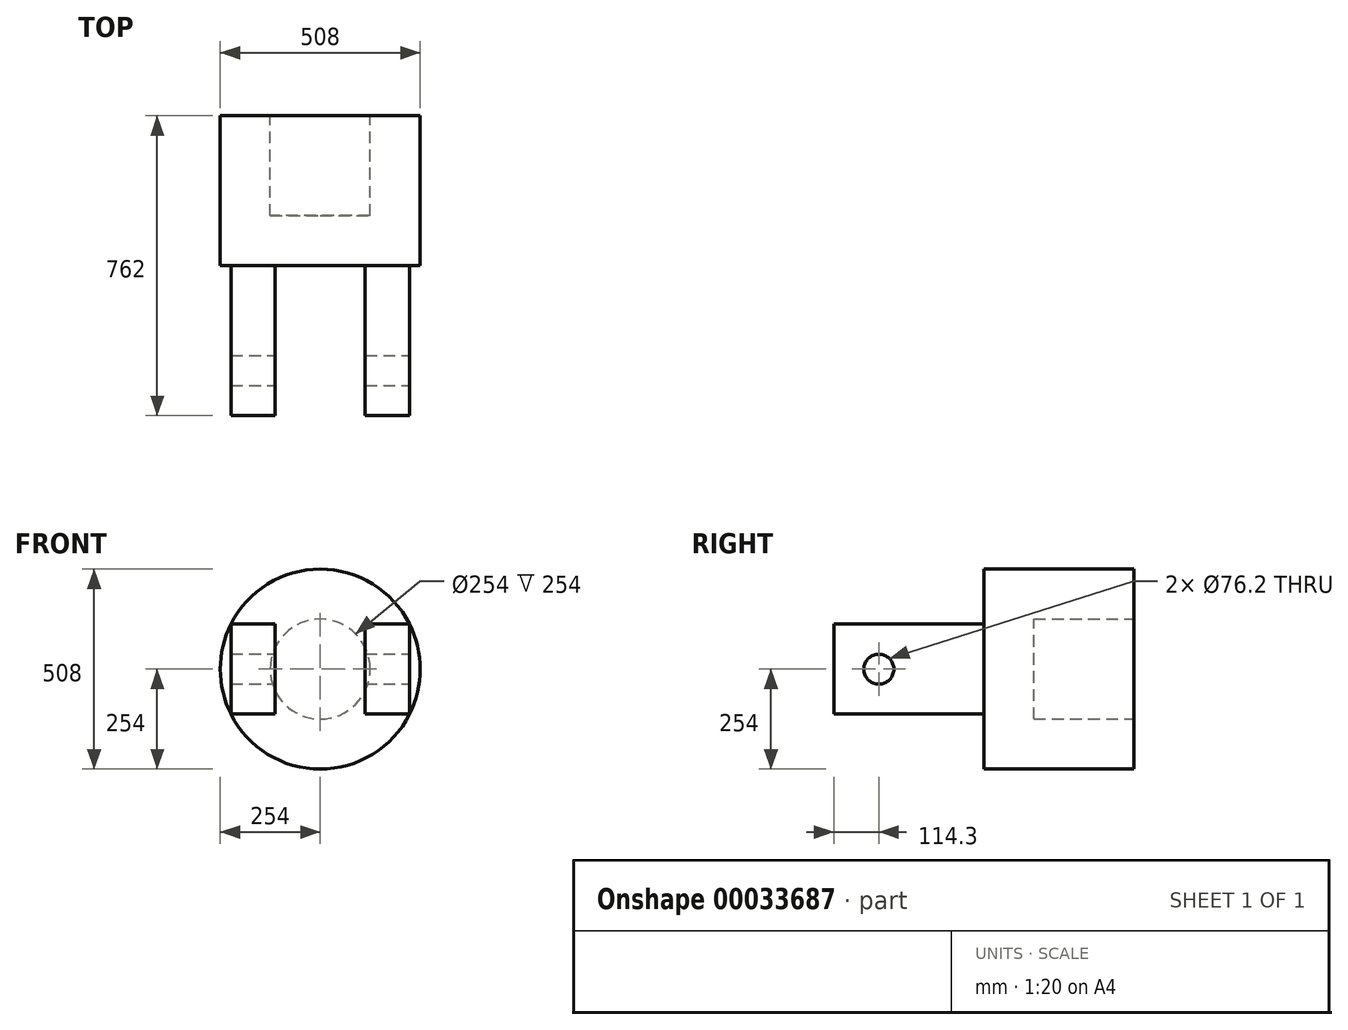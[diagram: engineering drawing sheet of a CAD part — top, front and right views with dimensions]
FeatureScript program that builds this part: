
annotation { "Feature Type Name" : "Feature", "Feature Type Description" : "" }
export const myFeature = defineFeature(function(context is Context, id is Id, definition is map)
    precondition{}
    {
        {
            var Q0;
            Q0=qCreatedBy(makeId("Front.planeOp"),FACE);
            var sketch = newSketch(context, id + "F0", { "sketchPlane" : qUnion([Q0])});
            skCircle(sketch, "E0", {"center": v(0, 0) * mm, "radius": 127 * mm});
            skCircle(sketch, "E1", {"center": v(0, 0) * mm, "radius": 254 * mm});
            skSolve(sketch);
        }
        {
            var Q0;
            Q0 = qSketchRegion(id + "F0", true);
            extrude(context, id + "F1", {"entities" : qUnion([Q0]), "depth" : 254 * mm});
        }
        {
            var Q0;
            Q0=makeQuery(id+"F1.opExtrude","CAP_FACE",FACE,{"disambiguationData":[OSD([sQuery(id+"F0.wireOp",EDGE,"E0"),sQuery(id+"F0.wireOp",EDGE,"E1")])],"isStart":false});
            var sketch = newSketch(context, id + "F2", { "sketchPlane" : qUnion([Q0])});
            skCircle(sketch, "E2", {"center": v(0, 0) * mm, "radius": 254 * mm});
            skSolve(sketch);
        }
        {
            var Q0;
            Q0 = qSketchRegion(id + "F2", true);
            extrude(context, id + "F3", {"entities" : qUnion([Q0]), "operationType" : NewBodyOperationType.ADD, "depth" : 127 * mm});
        }
        {
            var Q0;
            Q0=makeQuery(id+"F3.opExtrude","CAP_FACE",FACE,{"disambiguationData":[OSD([sQuery(id+"F2.wireOp",EDGE,"E2")])],"isStart":false});
            var sketch = newSketch(context, id + "F4", { "sketchPlane" : qUnion([Q0])});
            skLineSegment(sketch, "E3.bottom", {"start": v(-226.83, 114.3) * mm, "end": v(-114.3, 114.3) * mm});
            skLineSegment(sketch, "E3.top", {"start": v(-226.83, -114.3) * mm, "end": v(-114.3, -114.3) * mm});
            skLineSegment(sketch, "E3.left", {"start": v(-226.83, 114.3) * mm, "end": v(-226.83, -114.3) * mm});
            skLineSegment(sketch, "E3.right", {"start": v(-114.3, 114.3) * mm, "end": v(-114.3, -114.3) * mm});
            skLineSegment(sketch, "E4.bottom", {"start": v(114.3, 114.3) * mm, "end": v(226.83, 114.3) * mm});
            skLineSegment(sketch, "E4.top", {"start": v(114.3, -114.3) * mm, "end": v(226.83, -114.3) * mm});
            skLineSegment(sketch, "E4.left", {"start": v(114.3, 114.3) * mm, "end": v(114.3, -114.3) * mm});
            skLineSegment(sketch, "E4.right", {"start": v(226.83, 114.3) * mm, "end": v(226.83, -114.3) * mm});
            skSolve(sketch);
        }
        {
            var Q0;
            Q0 = qSketchRegion(id + "F4", true);
            extrude(context, id + "F5", {"entities" : qUnion([Q0]), "operationType" : NewBodyOperationType.ADD, "depth" : 381 * mm});
        }
        {
            var Q0;
            Q0=makeQuery(id+"F5.opExtrude","SWEPT_FACE",FACE,{"disambiguationData":[OSD([sQuery(id+"F4.wireOp",EDGE,"E4.right")])]});
            var sketch = newSketch(context, id + "F6", { "sketchPlane" : qUnion([Q0])});
            skCircle(sketch, "E5", {"center": v(-647.7, 0) * mm, "radius": 38.1 * mm});
            skSolve(sketch);
        }
        {
            var Q0;
            Q0 = qSketchRegion(id + "F6", true);
            extrude(context, id + "F7", {"entities" : qUnion([Q0]), "operationType" : NewBodyOperationType.REMOVE, "endBound" : BoundingType.THROUGH_ALL, "oppositeDirection" : true, "depth" : 25.4 * mm});
        }
    });
